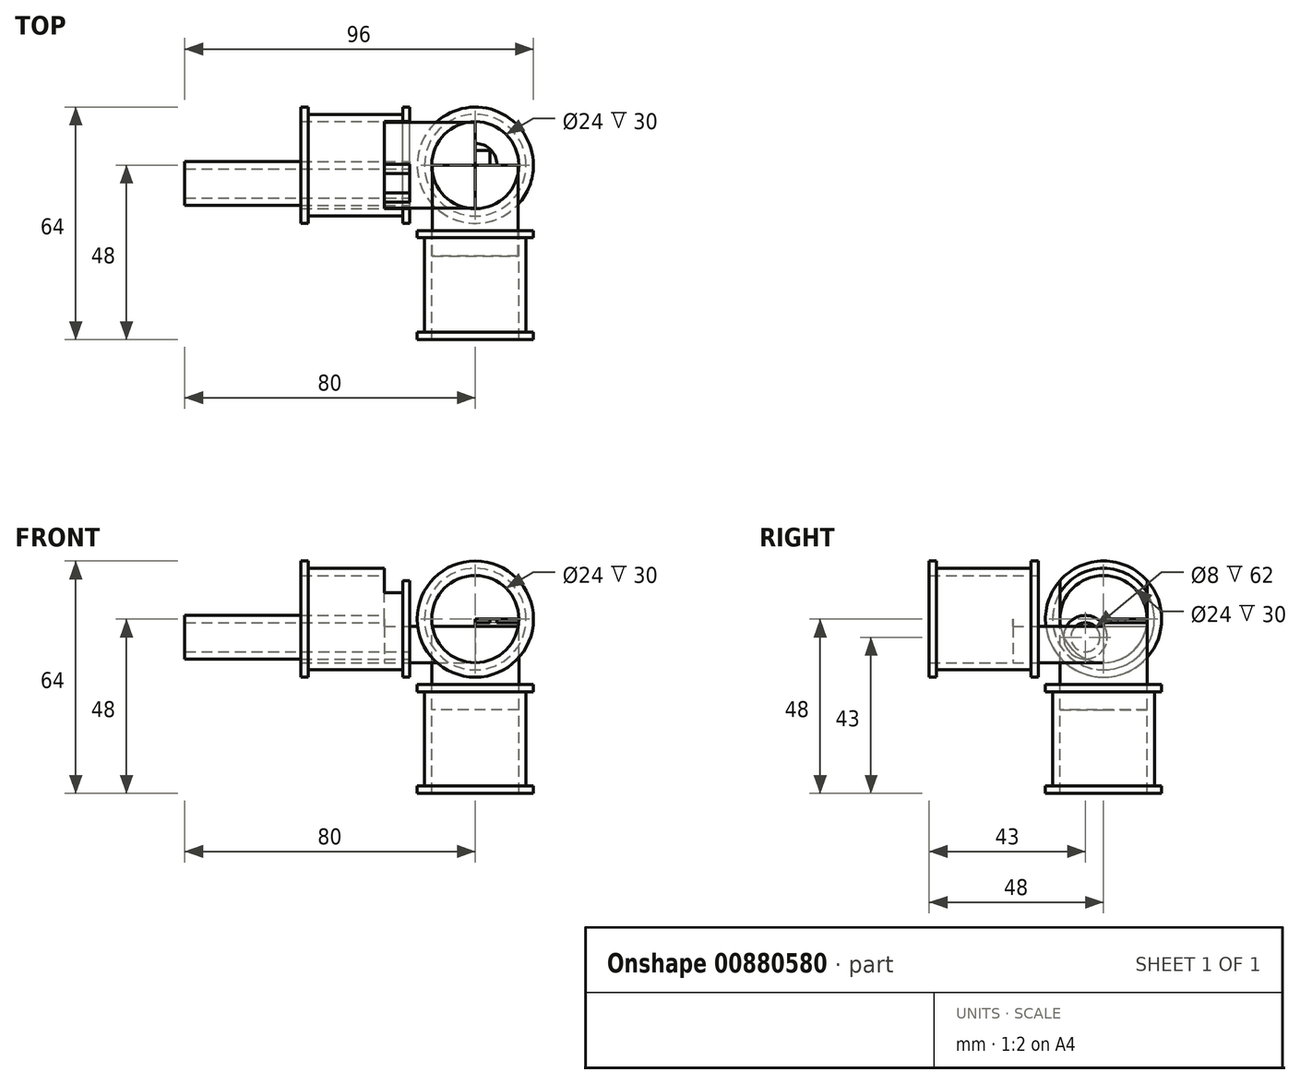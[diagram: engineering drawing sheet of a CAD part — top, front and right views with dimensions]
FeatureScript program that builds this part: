
annotation { "Feature Type Name" : "Feature", "Feature Type Description" : "" }
export const myFeature = defineFeature(function(context is Context, id is Id, definition is map)
    precondition{}
    {
        {
            var Q0;
            Q0=qCreatedBy(makeId("Top.planeOp"),FACE);
            var sketch = newSketch(context, id + "F0", { "sketchPlane" : qUnion([Q0])});
            skLineSegment(sketch, "E0.bottom", {"start": v(4, 4) * mm, "end": v(-4, 4) * mm});
            skLineSegment(sketch, "E0.top", {"start": v(4, -4) * mm, "end": v(-4, -4) * mm});
            skLineSegment(sketch, "E0.left", {"start": v(4, 4) * mm, "end": v(4, -4) * mm});
            skLineSegment(sketch, "E0.right", {"start": v(-4, 4) * mm, "end": v(-4, -4) * mm});
            skPoint(sketch, "E0.middle", {"position": v(0, 0) * mm});
            skCircle(sketch, "E1", {"center": v(0, 0) * mm, "radius": 16 * mm});
            skCircle(sketch, "E2", {"center": v(0, 0) * mm, "radius": 14 * mm});
            skCircle(sketch, "E3", {"center": v(0, 0) * mm, "radius": 12 * mm});
            skCircle(sketch, "E4", {"center": v(0, 0) * mm, "radius": 6 * mm});
            skSolve(sketch);
        }
        {
            var Q0;
            Q0=qCreatedBy(makeId("Right.planeOp"),FACE);
            var sketch = newSketch(context, id + "F1", { "sketchPlane" : qUnion([Q0])});
            skCircle(sketch, "E5", {"center": v(0, 0) * mm, "radius": 16 * mm});
            skCircle(sketch, "E6", {"center": v(0, 0) * mm, "radius": 14 * mm});
            skCircle(sketch, "E7", {"center": v(0, 0) * mm, "radius": 12 * mm});
            skLineSegment(sketch, "E8", {"start": v(-12, 0) * mm, "end": v(12, 0) * mm});
            skSolve(sketch);
        }
        {
            var Q0;
            Q0=qCreatedBy(makeId("Front.planeOp"),FACE);
            var sketch = newSketch(context, id + "F2", { "sketchPlane" : qUnion([Q0])});
            skCircle(sketch, "E9", {"center": v(0, 0) * mm, "radius": 16 * mm});
            skCircle(sketch, "E10", {"center": v(0, 0) * mm, "radius": 14 * mm});
            skCircle(sketch, "E11", {"center": v(0, 0) * mm, "radius": 12 * mm});
            skLineSegment(sketch, "E12", {"start": v(12, 0) * mm, "end": v(-12, 0) * mm});
            skSolve(sketch);
        }
        {
            var Q0;
            Q0=makeQuery(id+"F0.imprint","IMPRINT",FACE,{"disambiguationData":[TD([[makeQuery(id+"F0.imprint","IMPRINT",EDGE,{"derivedFrom":sQuery(id+"F0.wireOp",EDGE,"E1")}),1.0]])]});
            extrude(context, id + "F3", {"entities" : qUnion([Q0]), "oppositeDirection" : true, "depth" : 46 * mm, "offsetDistance" : 25 * mm, "hasSecondDirection" : true, "secondDirectionOppositeDirection" : true, "secondDirectionDepth" : 20 * mm});
        }
        {
            var Q0;
            Q0=makeQuery(id+"F1.imprint","IMPRINT",FACE,{"disambiguationData":[TD([[makeQuery(id+"F1.imprint","IMPRINT",EDGE,{"derivedFrom":sQuery(id+"F1.wireOp",EDGE,"E5")}),1.0]])]});
            extrude(context, id + "F4", {"entities" : qUnion([Q0]), "oppositeDirection" : true, "depth" : 46 * mm, "offsetDistance" : 25 * mm, "hasSecondDirection" : true, "secondDirectionOppositeDirection" : true, "secondDirectionDepth" : 20 * mm});
        }
        {
            var Q0;
            Q0=makeQuery(id+"F2.imprint","IMPRINT",FACE,{"disambiguationData":[TD([[makeQuery(id+"F2.imprint","IMPRINT",EDGE,{"derivedFrom":sQuery(id+"F2.wireOp",EDGE,"E9")}),1.0]])]});
            extrude(context, id + "F5", {"entities" : qUnion([Q0]), "depth" : 46 * mm, "offsetDistance" : 25 * mm, "hasSecondDirection" : true, "secondDirectionOppositeDirection" : false, "secondDirectionDepth" : 20 * mm});
        }
        {
            var Q0;
            Q0=makeQuery(id+"F2.imprint","IMPRINT",FACE,{"disambiguationData":[TD([[makeQuery(id+"F2.imprint","IMPRINT",EDGE,{"derivedFrom":sQuery(id+"F2.wireOp",EDGE,"E10")}),1.0]])]});
            var Q1;
            Q1=makeQuery(id+"F2.imprint","IMPRINT",FACE,{"disambiguationData":[TD([[makeQuery(id+"F2.imprint","IMPRINT",EDGE,{"derivedFrom":sQuery(id+"F2.wireOp",EDGE,"E9")}),1.0]])]});
            extrude(context, id + "F6", {"entities" : qUnion([Q0, Q1]), "depth" : 48 * mm, "offsetDistance" : 25 * mm, "hasSecondDirection" : true, "secondDirectionOppositeDirection" : false, "secondDirectionDepth" : 18 * mm});
        }
        {
            var Q0;
            Q0=makeQuery(id+"F1.imprint","IMPRINT",FACE,{"disambiguationData":[TD([[makeQuery(id+"F1.imprint","IMPRINT",EDGE,{"derivedFrom":sQuery(id+"F1.wireOp",EDGE,"E6")}),1.0]])]});
            var Q1;
            Q1=makeQuery(id+"F1.imprint","IMPRINT",FACE,{"disambiguationData":[TD([[makeQuery(id+"F1.imprint","IMPRINT",EDGE,{"derivedFrom":sQuery(id+"F1.wireOp",EDGE,"E5")}),1.0]])]});
            extrude(context, id + "F7", {"entities" : qUnion([Q0, Q1]), "oppositeDirection" : true, "depth" : 48 * mm, "offsetDistance" : 25 * mm, "hasSecondDirection" : true, "secondDirectionOppositeDirection" : true, "secondDirectionDepth" : 18 * mm});
        }
        {
            var Q0;
            Q0=makeQuery(id+"F0.imprint","IMPRINT",FACE,{"disambiguationData":[TD([[makeQuery(id+"F0.imprint","IMPRINT",EDGE,{"derivedFrom":sQuery(id+"F0.wireOp",EDGE,"E2")}),1.0]])]});
            var Q1;
            Q1=makeQuery(id+"F0.imprint","IMPRINT",FACE,{"disambiguationData":[TD([[makeQuery(id+"F0.imprint","IMPRINT",EDGE,{"derivedFrom":sQuery(id+"F0.wireOp",EDGE,"E1")}),1.0]])]});
            extrude(context, id + "F8", {"entities" : qUnion([Q0, Q1]), "oppositeDirection" : true, "depth" : 48 * mm, "offsetDistance" : 25 * mm, "hasSecondDirection" : true, "secondDirectionOppositeDirection" : true, "secondDirectionDepth" : 18 * mm});
        }
        {
            var Q0;
            Q0=makeQuery(id+"F0.imprint","IMPRINT",FACE,{"disambiguationData":[TD([[makeQuery(id+"F0.imprint","IMPRINT",EDGE,{"derivedFrom":sQuery(id+"F0.wireOp",EDGE,"YIG0J7lI-ZUaQ-ceel-rp2b-WwoC8Ox2qIIC")}),-1.0]])]});
            var Q1;
            Q1=makeQuery(id+"F0.imprint","IMPRINT",FACE,{"disambiguationData":[TD([[makeQuery(id+"F0.imprint","IMPRINT",EDGE,{"derivedFrom":sQuery(id+"F0.wireOp",EDGE,"E0.bottom")}),-1.0]])]});
            var Q2;
            Q2=makeQuery(id+"F0.imprint","IMPRINT",FACE,{"disambiguationData":[TD([[makeQuery(id+"F0.imprint","IMPRINT",EDGE,{"derivedFrom":sQuery(id+"F0.wireOp",EDGE,"E0.bottom")}),1.0]])]});
            var Q3;
            Q3=makeQuery(id+"F0.imprint","IMPRINT",FACE,{"disambiguationData":[TD([[makeQuery(id+"F0.imprint","IMPRINT",EDGE,{"derivedFrom":sQuery(id+"F0.wireOp",EDGE,"E3")}),1.0]])]});
            extrude(context, id + "F9", {"entities" : qUnion([Q0, Q1, Q2, Q3]), "oppositeDirection" : true, "depth" : 25 * mm, "offsetDistance" : 25 * mm});
        }
        {
            var Q0;
            Q0=makeQuery(id+"F0.imprint","IMPRINT",FACE,{"disambiguationData":[TD([[makeQuery(id+"F0.imprint","IMPRINT",EDGE,{"derivedFrom":sQuery(id+"F0.wireOp",EDGE,"E0.bottom")}),1.0]])]});
            var Q1;
            Q1=makeQuery(id+"F0.imprint","IMPRINT",FACE,{"disambiguationData":[TD([[makeQuery(id+"F0.imprint","IMPRINT",EDGE,{"derivedFrom":sQuery(id+"F0.wireOp",EDGE,"E3")}),1.0]])]});
            extrude(context, id + "F10", {"entities" : qUnion([Q0, Q1]), "operationType" : NewBodyOperationType.REMOVE, "oppositeDirection" : true, "depth" : 1 * mm, "offsetDistance" : 25 * mm});
        }
        {
            var Q0;
            Q0=makeQuery(id+"F0.imprint","IMPRINT",FACE,{"disambiguationData":[TD([[makeQuery(id+"F0.imprint","IMPRINT",EDGE,{"derivedFrom":sQuery(id+"F0.wireOp",EDGE,"E3")}),1.0]])]});
            extrude(context, id + "F11", {"entities" : qUnion([Q0]), "oppositeDirection" : true, "depth" : 1 * mm, "offsetDistance" : 25 * mm});
        }
        {
            var Q0;
            {var subQ0=sQuery(id+"F2.wireOp",EDGE,"E12");Q0=makeQuery(id+"F2.imprint","IMPRINT",FACE,{"disambiguationData":[TD([[makeQuery(id+"F2.imprint","IMPRINT",EDGE,{"derivedFrom":subQ0}),1.0]])]});}
            extrude(context, id + "F12", {"entities" : qUnion([Q0]), "depth" : 25 * mm, "offsetDistance" : 25 * mm});
        }
        {
            var Q0;
            Q0=makeQuery(id+"F12.opExtrude","SWEPT_FACE",FACE,{"disambiguationData":[OSD([sQuery(id+"F2.wireOp",EDGE,"E12")])]});
            extrude(context, id + "F13", {"entities" : qUnion([Q0]), "operationType" : NewBodyOperationType.REMOVE, "oppositeDirection" : true, "depth" : 2 * mm, "offsetDistance" : 25 * mm});
        }
        {
            var Q0;
            {var subQ0=sQuery(id+"F1.wireOp",EDGE,"E8");Q0=makeQuery(id+"F1.imprint","IMPRINT",FACE,{"disambiguationData":[TD([[makeQuery(id+"F1.imprint","IMPRINT",EDGE,{"derivedFrom":subQ0}),-1.0]])]});}
            extrude(context, id + "F14", {"entities" : qUnion([Q0]), "oppositeDirection" : true, "depth" : 25 * mm, "offsetDistance" : 25 * mm});
        }
        {
            var Q0;
            Q0=qCreatedBy(makeId("Right.planeOp"),FACE);
            var sketch = newSketch(context, id + "F15", { "sketchPlane" : qUnion([Q0])});
            skCircle(sketch, "E13", {"center": v(-5, -5) * mm, "radius": 6 * mm});
            skCircle(sketch, "E14", {"center": v(-5, -5) * mm, "radius": 4 * mm});
            skSolve(sketch);
        }
        {
            var Q0;
            Q0 = qSketchRegion(id + "F15", true);
            var Q1;
            Q1=makeQuery(id+"F15.imprint","IMPRINT",FACE,{"disambiguationData":[TD([[makeQuery(id+"F15.imprint","IMPRINT",EDGE,{"derivedFrom":sQuery(id+"F15.wireOp",EDGE,"E14")}),1.0]])]});
            extrude(context, id + "F16", {"entities" : qUnion([Q0, Q1]), "oppositeDirection" : true, "depth" : 80 * mm, "offsetDistance" : 25 * mm, "hasSecondDirection" : true, "secondDirectionOppositeDirection" : true, "secondDirectionDepth" : 18 * mm});
        }
        {
            var Q0;
            Q0=makeQuery(id+"F14.opExtrude","SWEPT_FACE",FACE,{"disambiguationData":[OSD([sQuery(id+"F1.wireOp",EDGE,"E8")])]});
            extrude(context, id + "F17", {"entities" : qUnion([Q0]), "operationType" : NewBodyOperationType.REMOVE, "oppositeDirection" : true, "depth" : 2 * mm, "offsetDistance" : 25 * mm, "hasSecondDirection" : true, "secondDirectionOppositeDirection" : false, "secondDirectionDepth" : 25 * mm});
        }
        {
            var Q0;
            Q0=makeQuery(id+"F5.opExtrude","SWEPT_BODY",BODY,{"disambiguationData":[OSD([sQuery(id+"F2.wireOp",EDGE,"E9"),sQuery(id+"F2.wireOp",EDGE,"E10")])]});
            var Q1;
            Q1=makeQuery(id+"F6.opExtrude","SWEPT_BODY",BODY,{"disambiguationData":[OSD([sQuery(id+"F2.wireOp",EDGE,"E9"),sQuery(id+"F2.wireOp",EDGE,"E11")])]});
            booleanBodies(context, id + "F18", {"operationType" : BooleanOperationType.SUBTRACTION, "tools" : qUnion([Q0]), "targets" : qUnion([Q1])});
        }
        {
            var Q0;
            Q0=makeQuery(id+"F4.opExtrude","SWEPT_BODY",BODY,{"disambiguationData":[OSD([sQuery(id+"F1.wireOp",EDGE,"E5"),sQuery(id+"F1.wireOp",EDGE,"E6")])]});
            var Q1;
            Q1=makeQuery(id+"F7.opExtrude","SWEPT_BODY",BODY,{"disambiguationData":[OSD([sQuery(id+"F1.wireOp",EDGE,"E5"),sQuery(id+"F1.wireOp",EDGE,"E7")])]});
            booleanBodies(context, id + "F19", {"operationType" : BooleanOperationType.SUBTRACTION, "tools" : qUnion([Q0]), "targets" : qUnion([Q1])});
        }
        {
            var Q0;
            Q0=makeQuery(id+"F3.opExtrude","SWEPT_BODY",BODY,{"disambiguationData":[OSD([sQuery(id+"F0.wireOp",EDGE,"E1"),sQuery(id+"F0.wireOp",EDGE,"E2")])]});
            var Q1;
            Q1=makeQuery(id+"F8.opExtrude","SWEPT_BODY",BODY,{"disambiguationData":[OSD([sQuery(id+"F0.wireOp",EDGE,"E1"),sQuery(id+"F0.wireOp",EDGE,"E3")])]});
            booleanBodies(context, id + "F20", {"operationType" : BooleanOperationType.SUBTRACTION, "tools" : qUnion([Q0]), "targets" : qUnion([Q1])});
        }
        {
            var Q0;
            Q0=makeQuery(id+"F15.imprint","IMPRINT",FACE,{"disambiguationData":[TD([[makeQuery(id+"F15.imprint","IMPRINT",EDGE,{"derivedFrom":sQuery(id+"F15.wireOp",EDGE,"E14")}),1.0]])]});
            extrude(context, id + "F21", {"entities" : qUnion([Q0]), "operationType" : NewBodyOperationType.REMOVE, "oppositeDirection" : true, "depth" : 80 * mm, "offsetDistance" : 25 * mm, "hasSecondDirection" : true, "secondDirectionOppositeDirection" : true, "secondDirectionDepth" : 18 * mm});
        }
    });
